# Revit family: 1071xxx Imola 900 LED 0-10V
name_source: partatom
category: Lighting Fixtures
revit_build: Autodesk Revit 2018 (Build: 20170223_1515(x64)
units: mm (PartAtom-declared; Revit-internal decimal feet)

## family parameters
Always vertical = Yes
Cut with Voids When Loaded = No
Host = Wall
Light Source = Yes
OmniClass Number = 23.80.70.00
OmniClass Title = Lighting
Part Type = Normal
Room Calculation Point = No
Round Connector Dimension = Use Diameter
Shared = No

## types (1)
- Astro Imola 900 LED 0-10V
    ADA compliant = Yes
Yes
    Apparent Load = 14 VA
    Color Filter = 16777215
    Dimmable = Yes
    Dimming Lamp Color Temperature Shift = <None>
    Dimming Method = 0-10V
    Driver Included = Yes
    Driver Required = No
    Efficacy (lm/w) = 34
    Electrical Class = 1
    Lamp = Mid-Power LED
    Light Source Fixed = Yes
    Location / IP Rating = Damp
    Main Finish = Mirror
    Main Material = Glass - Float
    Manufacturer = Astro Lighting Ltd
    Manufacturer URL - Europe and Rest of World = www.astrolighting.com
    Manufacturer URL - North America = us.astrolighting.com
    Photometric Web File = 1071012_Imola 900 LED 0-10V_Photometry_IES_Iss. 01.ies
    Power (Watts) = 13.7
    Product CCT = 3000K
    Product CRI = 80
    Product Dimensions (MM) = 900x600x42
    Product Location = Bathroom
    Product Name = Imola 900 LED 0-10V
    Product SKU = 1071012
    Product URL = https://us.astrolighting.com
    Product Weight (KG) = 9.96
    Tilt Angle = 0.00°
    URL = www.astrolighting.com

## geometry (parser evidence)
native form markers: Sweep x2
no freeform markers — native parametric forms only
